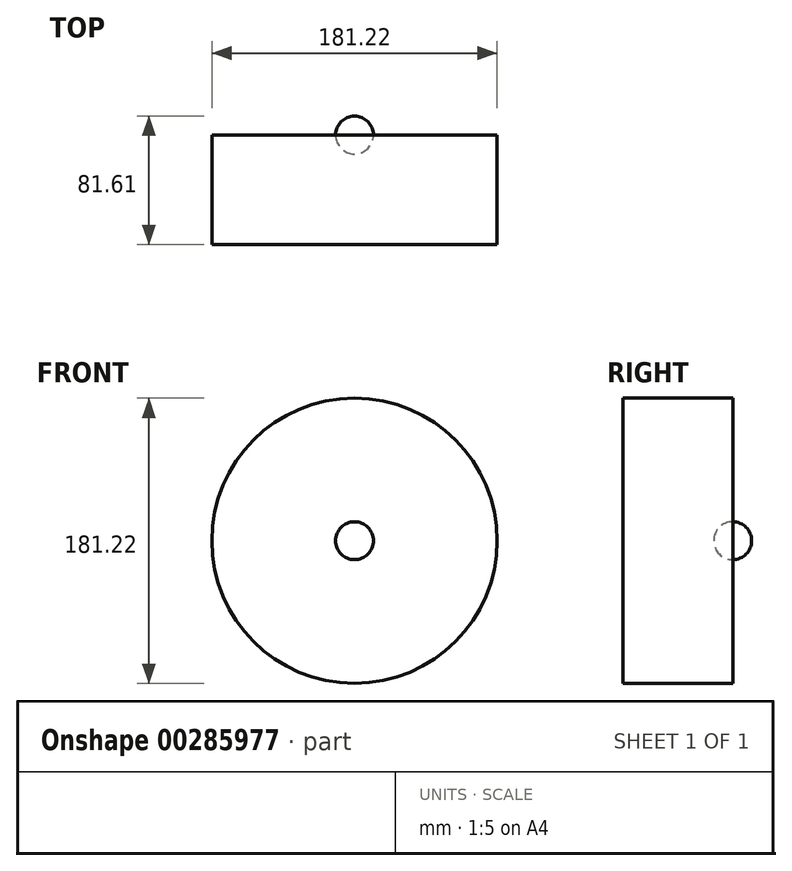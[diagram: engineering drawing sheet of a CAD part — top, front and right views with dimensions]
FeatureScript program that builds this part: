
annotation { "Feature Type Name" : "Feature", "Feature Type Description" : "" }
export const myFeature = defineFeature(function(context is Context, id is Id, definition is map)
    precondition{}
    {
        {
            var Q0;
            Q0=qCreatedBy(makeId("Front.planeOp"),FACE);
            var sketch = newSketch(context, id + "F0", { "sketchPlane" : qUnion([Q0])});
            skCircle(sketch, "E0", {"center": v(0, 0) * mm, "radius": 90.61 * mm});
            skCircle(sketch, "E1", {"center": v(0, 0) * mm, "radius": 71.54 * mm});
            skCircle(sketch, "E2", {"center": v(0, 0) * mm, "radius": 55.37 * mm});
            skArc(sketch, "E3", {"start": v(-8.14, 38.86) * mm, "mid": v(-1.06, -39.7) * mm, "end": v(10.2, 38.37) * mm});
            skCircle(sketch, "E4", {"center": v(0, 0) * mm, "radius": 23.75 * mm});
            skArc(sketch, "E5", {"start": v(0, -12.01) * mm, "mid": v(12.01, 0) * mm, "end": v(0, 12.01) * mm});
            skLineSegment(sketch, "E6", {"start": v(0, 112.78) * mm, "end": v(0, -148.75) * mm, "construction": true});
            skLineSegment(sketch, "E7", {"start": v(-11.12, 43.94) * mm, "end": v(-4.87, 33.27) * mm, "construction": true});
            skLineSegment(sketch, "E8", {"start": v(-4.87, 33.27) * mm, "end": v(15.18, 40.06) * mm, "construction": true});
            skSolve(sketch);
        }
        {
            var Q0;
            Q0=sQuery(id+"F0.wireOp",EDGE,"E0");
            extrude(context, id + "F1", {"bodyType" : ToolBodyType.SURFACE, "surfaceEntities" : qUnion([Q0]), "depth" : 69.6 * mm});
        }
        {
            var Q0;
            Q0=sQuery(id+"F0.wireOp",EDGE,"E5");
            var Q1;
            Q1=sQuery(id+"F0.wireOp",EDGE,"E6");
            revolve(context, id + "F2", {"bodyType" : ToolBodyType.SURFACE, "surfaceEntities" : qUnion([Q0]), "axis" : qUnion([Q1]), "revolveType" : RevolveType.FULL});
        }
        {
            var Q0;
            Q0=sQuery(id+"F0.wireOp",EDGE,"E3");
            var Q1;
            Q1=sQuery(id+"F0.wireOp",VERTEX,"E3.start");
            cPlane(context, id + "F3", {"entities" : qUnion([Q0, Q1]), "cplaneType" : CPlaneType.CURVE_POINT, "offset" : 25.4 * mm, "width" : 152.4 * mm, "height" : 152.4 * mm});
        }
        {
            var Q0;
            Q0=qCreatedBy(id+"F3.planeOp",FACE);
            var sketch = newSketch(context, id + "F4", { "sketchPlane" : qUnion([Q0])});
            skCircle(sketch, "E9", {"center": v(0, 39.7) * mm, "radius": 8.5 * mm});
            skSolve(sketch);
        }
    });
